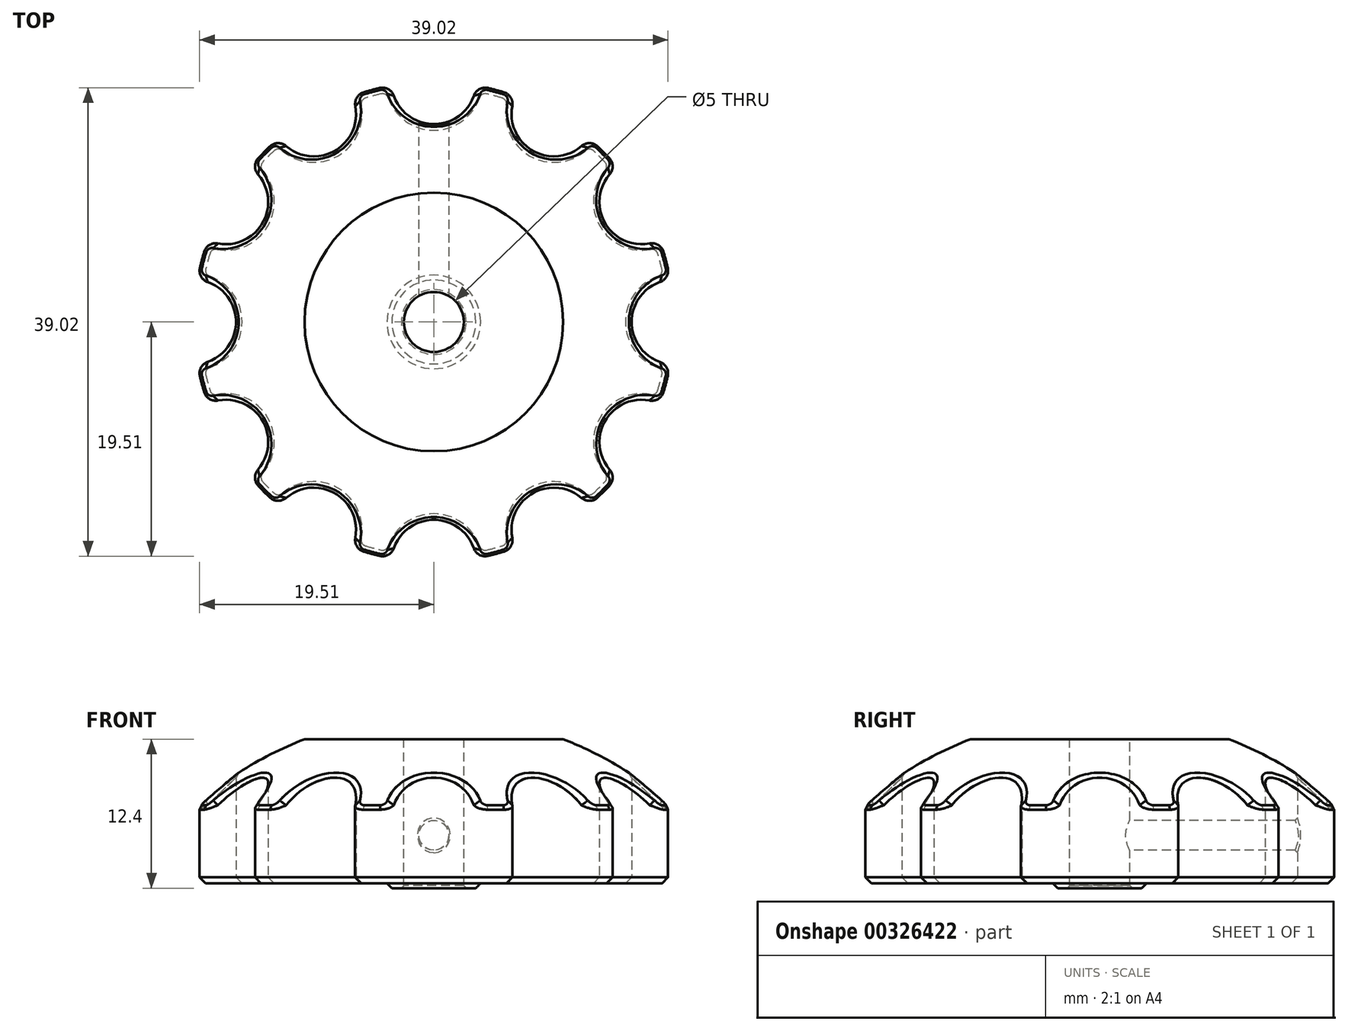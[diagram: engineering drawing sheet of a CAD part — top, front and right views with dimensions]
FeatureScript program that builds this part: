
annotation { "Feature Type Name" : "Feature", "Feature Type Description" : "" }
export const myFeature = defineFeature(function(context is Context, id is Id, definition is map)
    precondition{}
    {
        {
            var Q0;
            Q0=qCreatedBy(makeId("Top.planeOp"),FACE);
            var sketch = newSketch(context, id + "F0", { "sketchPlane" : qUnion([Q0])});
            skLineSegment(sketch, "E0", {"start": v(0, 0) * mm, "end": v(-20, 0) * mm, "construction": true});
            skArc(sketch, "E1", {"start": v(-19.49, -4.5) * mm, "mid": v(-19.32, -5.18) * mm, "end": v(-19.13, -5.85) * mm});
            skArc(sketch, "E2", {"start": v(-18.84, -3.33) * mm, "mid": v(-16.47, 0) * mm, "end": v(-18.84, 3.33) * mm});
            skArc(sketch, "E3", {"start": v(-19.49, 4.5) * mm, "mid": v(-19.39, 3.8) * mm, "end": v(-18.84, 3.33) * mm});
            skPoint(sketch, "E4", {"position": v(-18.84, 3.33) * mm});
            skLineSegment(sketch, "E5", {"start": v(0, 0) * mm, "end": v(-18.51, 4.27) * mm, "construction": true});
            skLineSegment(sketch, "E6.MirrorCS", {"start": v(0, 0) * mm, "end": v(-18.51, -4.27) * mm, "construction": true});
            skArc(sketch, "E7.MirrorCS", {"start": v(-19.49, -4.5) * mm, "mid": v(-19.39, -3.8) * mm, "end": v(-18.84, -3.33) * mm});
            skArc(sketch, "E8.1.0", {"start": v(-19.13, -5.85) * mm, "mid": v(-18.69, -6.41) * mm, "end": v(-17.98, -6.54) * mm});
            skArc(sketch, "E8.1.1", {"start": v(-14.65, -12.3) * mm, "mid": v(-14.27, -8.24) * mm, "end": v(-17.98, -6.54) * mm});
            skArc(sketch, "E8.1.2", {"start": v(-14.63, -13.64) * mm, "mid": v(-14.9, -12.98) * mm, "end": v(-14.65, -12.3) * mm});
            skArc(sketch, "E8.2.0", {"start": v(-13.64, -14.63) * mm, "mid": v(-12.98, -14.9) * mm, "end": v(-12.3, -14.65) * mm});
            skArc(sketch, "E8.2.1", {"start": v(-6.54, -17.98) * mm, "mid": v(-8.24, -14.27) * mm, "end": v(-12.3, -14.65) * mm});
            skArc(sketch, "E8.2.2", {"start": v(-5.85, -19.13) * mm, "mid": v(-6.41, -18.69) * mm, "end": v(-6.54, -17.98) * mm});
            skArc(sketch, "E8.3.0", {"start": v(-4.5, -19.49) * mm, "mid": v(-3.8, -19.39) * mm, "end": v(-3.33, -18.84) * mm});
            skArc(sketch, "E8.3.1", {"start": v(3.33, -18.84) * mm, "mid": v(0, -16.47) * mm, "end": v(-3.33, -18.84) * mm});
            skArc(sketch, "E8.3.2", {"start": v(4.5, -19.49) * mm, "mid": v(3.8, -19.39) * mm, "end": v(3.33, -18.84) * mm});
            skArc(sketch, "E8.4.0", {"start": v(5.85, -19.13) * mm, "mid": v(6.41, -18.69) * mm, "end": v(6.54, -17.98) * mm});
            skArc(sketch, "E8.4.1", {"start": v(12.3, -14.65) * mm, "mid": v(8.24, -14.27) * mm, "end": v(6.54, -17.98) * mm});
            skArc(sketch, "E8.4.2", {"start": v(13.64, -14.63) * mm, "mid": v(12.98, -14.9) * mm, "end": v(12.3, -14.65) * mm});
            skArc(sketch, "E8.5.0", {"start": v(14.63, -13.64) * mm, "mid": v(14.9, -12.98) * mm, "end": v(14.65, -12.3) * mm});
            skArc(sketch, "E8.5.1", {"start": v(17.98, -6.54) * mm, "mid": v(14.27, -8.24) * mm, "end": v(14.65, -12.3) * mm});
            skArc(sketch, "E8.5.2", {"start": v(19.13, -5.85) * mm, "mid": v(18.69, -6.41) * mm, "end": v(17.98, -6.54) * mm});
            skArc(sketch, "E8.6.0", {"start": v(19.49, -4.5) * mm, "mid": v(19.39, -3.8) * mm, "end": v(18.84, -3.33) * mm});
            skArc(sketch, "E8.6.1", {"start": v(18.84, 3.33) * mm, "mid": v(16.47, 0) * mm, "end": v(18.84, -3.33) * mm});
            skArc(sketch, "E8.6.2", {"start": v(19.49, 4.5) * mm, "mid": v(19.39, 3.8) * mm, "end": v(18.84, 3.33) * mm});
            skArc(sketch, "E8.7.0", {"start": v(19.13, 5.85) * mm, "mid": v(18.69, 6.41) * mm, "end": v(17.98, 6.54) * mm});
            skArc(sketch, "E8.7.1", {"start": v(14.65, 12.3) * mm, "mid": v(14.27, 8.24) * mm, "end": v(17.98, 6.54) * mm});
            skArc(sketch, "E8.7.2", {"start": v(14.63, 13.64) * mm, "mid": v(14.9, 12.98) * mm, "end": v(14.65, 12.3) * mm});
            skArc(sketch, "E8.8.0", {"start": v(13.64, 14.63) * mm, "mid": v(12.98, 14.9) * mm, "end": v(12.3, 14.65) * mm});
            skArc(sketch, "E8.8.1", {"start": v(6.54, 17.98) * mm, "mid": v(8.24, 14.27) * mm, "end": v(12.3, 14.65) * mm});
            skArc(sketch, "E8.8.2", {"start": v(5.85, 19.13) * mm, "mid": v(6.41, 18.69) * mm, "end": v(6.54, 17.98) * mm});
            skArc(sketch, "E8.9.0", {"start": v(4.5, 19.49) * mm, "mid": v(3.8, 19.39) * mm, "end": v(3.33, 18.84) * mm});
            skArc(sketch, "E8.9.1", {"start": v(-3.33, 18.84) * mm, "mid": v(0, 16.47) * mm, "end": v(3.33, 18.84) * mm});
            skArc(sketch, "E8.9.2", {"start": v(-4.5, 19.49) * mm, "mid": v(-3.8, 19.39) * mm, "end": v(-3.33, 18.84) * mm});
            skArc(sketch, "E8.10.0", {"start": v(-5.85, 19.13) * mm, "mid": v(-6.41, 18.69) * mm, "end": v(-6.54, 17.98) * mm});
            skArc(sketch, "E8.10.1", {"start": v(-12.3, 14.65) * mm, "mid": v(-8.24, 14.27) * mm, "end": v(-6.54, 17.98) * mm});
            skArc(sketch, "E8.10.2", {"start": v(-13.64, 14.63) * mm, "mid": v(-12.98, 14.9) * mm, "end": v(-12.3, 14.65) * mm});
            skArc(sketch, "E8.11.0", {"start": v(-14.63, 13.64) * mm, "mid": v(-14.9, 12.98) * mm, "end": v(-14.65, 12.3) * mm});
            skArc(sketch, "E8.11.1", {"start": v(-17.98, 6.54) * mm, "mid": v(-14.27, 8.24) * mm, "end": v(-14.65, 12.3) * mm});
            skArc(sketch, "E8.11.2", {"start": v(-19.13, 5.85) * mm, "mid": v(-18.69, 6.41) * mm, "end": v(-17.98, 6.54) * mm});
            skArc(sketch, "E9.trimOffspring", {"start": v(-19.13, 5.85) * mm, "mid": v(-19.32, 5.18) * mm, "end": v(-19.49, 4.5) * mm});
            skArc(sketch, "E10.trimOffspring", {"start": v(-13.64, 14.63) * mm, "mid": v(-14.14, 14.14) * mm, "end": v(-14.63, 13.64) * mm});
            skArc(sketch, "E11.trimOffspring", {"start": v(-4.5, 19.49) * mm, "mid": v(-5.18, 19.32) * mm, "end": v(-5.85, 19.13) * mm});
            skArc(sketch, "E12.trimOffspring", {"start": v(5.85, 19.13) * mm, "mid": v(5.18, 19.32) * mm, "end": v(4.5, 19.49) * mm});
            skArc(sketch, "E13.trimOffspring", {"start": v(14.63, 13.64) * mm, "mid": v(14.14, 14.14) * mm, "end": v(13.64, 14.63) * mm});
            skArc(sketch, "E14.trimOffspring", {"start": v(19.49, 4.5) * mm, "mid": v(19.32, 5.18) * mm, "end": v(19.13, 5.85) * mm});
            skArc(sketch, "E15.trimOffspring", {"start": v(19.13, -5.85) * mm, "mid": v(19.32, -5.18) * mm, "end": v(19.49, -4.5) * mm});
            skArc(sketch, "E16.trimOffspring", {"start": v(13.64, -14.63) * mm, "mid": v(14.14, -14.14) * mm, "end": v(14.63, -13.64) * mm});
            skArc(sketch, "E17.trimOffspring", {"start": v(4.5, -19.49) * mm, "mid": v(5.18, -19.32) * mm, "end": v(5.85, -19.13) * mm});
            skArc(sketch, "E18.trimOffspring", {"start": v(-5.85, -19.13) * mm, "mid": v(-5.18, -19.32) * mm, "end": v(-4.5, -19.49) * mm});
            skArc(sketch, "E19.trimOffspring", {"start": v(-14.63, -13.64) * mm, "mid": v(-14.14, -14.14) * mm, "end": v(-13.64, -14.63) * mm});
            skSolve(sketch);
        }
        {
            var Q0;
            Q0 = qSketchRegion(id + "F0", true);
            extrude(context, id + "F1", {"entities" : qUnion([Q0]), "depth" : 12 * mm});
        }
        {
            var Q0;
            Q0=qCreatedBy(makeId("Front.planeOp"),FACE);
            var sketch = newSketch(context, id + "F2", { "sketchPlane" : qUnion([Q0])});
            skArc(sketch, "E20", {"start": v(25.38, 0) * mm, "mid": v(18.72, 7.44) * mm, "end": v(10, 12.28) * mm});
            skLineSegment(sketch, "E21", {"start": v(0, -16) * mm, "end": v(0, 0) * mm, "construction": true});
            skLineSegment(sketch, "E22", {"start": v(10, 14) * mm, "end": v(30, 14) * mm});
            skLineSegment(sketch, "E23", {"start": v(30, 14) * mm, "end": v(30, 0) * mm});
            skLineSegment(sketch, "E24", {"start": v(10, 12.28) * mm, "end": v(10, 14) * mm});
            skLineSegment(sketch, "E25", {"start": v(25.38, 0) * mm, "end": v(30, 0) * mm});
            skPoint(sketch, "E26.orphan", {"position": v(0, 14) * mm});
            skSolve(sketch);
        }
        {
            var Q0;
            Q0 = qSketchRegion(id + "F2", true);
            var Q1;
            Q1=sQuery(id+"F2.wireOp",EDGE,"E21");
            revolve(context, id + "F3", {"operationType" : NewBodyOperationType.REMOVE, "entities" : qUnion([Q0]), "axis" : qUnion([Q1]), "revolveType" : RevolveType.FULL, "oppositeDirection" : true});
        }
        {
            var Q0;
            Q0=makeQuery(id+"F1.opExtrude","CAP_FACE",FACE,{"disambiguationData":[OSD([sQuery(id+"F0.wireOp",EDGE,"E1"),sQuery(id+"F0.wireOp",EDGE,"E2"),sQuery(id+"F0.wireOp",EDGE,"E3"),sQuery(id+"F0.wireOp",EDGE,"E7.MirrorCS"),sQuery(id+"F0.wireOp",EDGE,"E8.1.0"),sQuery(id+"F0.wireOp",EDGE,"E8.1.1"),sQuery(id+"F0.wireOp",EDGE,"E8.1.2"),sQuery(id+"F0.wireOp",EDGE,"E8.2.0"),sQuery(id+"F0.wireOp",EDGE,"E8.2.1"),sQuery(id+"F0.wireOp",EDGE,"E8.2.2"),sQuery(id+"F0.wireOp",EDGE,"E8.3.0"),sQuery(id+"F0.wireOp",EDGE,"E8.3.1"),sQuery(id+"F0.wireOp",EDGE,"E8.3.2"),sQuery(id+"F0.wireOp",EDGE,"E8.4.0"),sQuery(id+"F0.wireOp",EDGE,"E8.4.1"),sQuery(id+"F0.wireOp",EDGE,"E8.4.2"),sQuery(id+"F0.wireOp",EDGE,"E8.5.0"),sQuery(id+"F0.wireOp",EDGE,"E8.5.1"),sQuery(id+"F0.wireOp",EDGE,"E8.5.2"),sQuery(id+"F0.wireOp",EDGE,"E8.6.0"),sQuery(id+"F0.wireOp",EDGE,"E8.6.1"),sQuery(id+"F0.wireOp",EDGE,"E8.6.2"),sQuery(id+"F0.wireOp",EDGE,"E8.7.0"),sQuery(id+"F0.wireOp",EDGE,"E8.7.1"),sQuery(id+"F0.wireOp",EDGE,"E8.7.2"),sQuery(id+"F0.wireOp",EDGE,"E8.8.0"),sQuery(id+"F0.wireOp",EDGE,"E8.8.1"),sQuery(id+"F0.wireOp",EDGE,"E8.8.2"),sQuery(id+"F0.wireOp",EDGE,"E8.9.0"),sQuery(id+"F0.wireOp",EDGE,"E8.9.1"),sQuery(id+"F0.wireOp",EDGE,"E8.9.2"),sQuery(id+"F0.wireOp",EDGE,"E8.10.0"),sQuery(id+"F0.wireOp",EDGE,"E8.10.1"),sQuery(id+"F0.wireOp",EDGE,"E8.10.2"),sQuery(id+"F0.wireOp",EDGE,"E8.11.0"),sQuery(id+"F0.wireOp",EDGE,"E8.11.1"),sQuery(id+"F0.wireOp",EDGE,"E8.11.2"),sQuery(id+"F0.wireOp",EDGE,"E9.trimOffspring"),sQuery(id+"F0.wireOp",EDGE,"E10.trimOffspring"),sQuery(id+"F0.wireOp",EDGE,"E11.trimOffspring"),sQuery(id+"F0.wireOp",EDGE,"E12.trimOffspring"),sQuery(id+"F0.wireOp",EDGE,"E13.trimOffspring"),sQuery(id+"F0.wireOp",EDGE,"E14.trimOffspring"),sQuery(id+"F0.wireOp",EDGE,"E15.trimOffspring"),sQuery(id+"F0.wireOp",EDGE,"E16.trimOffspring"),sQuery(id+"F0.wireOp",EDGE,"E17.trimOffspring"),sQuery(id+"F0.wireOp",EDGE,"E18.trimOffspring"),sQuery(id+"F0.wireOp",EDGE,"E19.trimOffspring")])],"isStart":false});
            var sketch = newSketch(context, id + "F4", { "sketchPlane" : qUnion([Q0])});
            skCircle(sketch, "E27", {"center": v(0, 0) * mm, "radius": 2.5 * mm});
            skSolve(sketch);
        }
        {
            var Q0;
            Q0=makeQuery(id+"F4.imprint","IMPRINT",FACE,{"disambiguationData":[TD([[makeQuery(id+"F4.imprint","IMPRINT",EDGE,{"derivedFrom":sQuery(id+"F4.wireOp",EDGE,"cDNHE1yy-ZxzA-wdTT-TKaF-RwySO2n7V80O")}),1.0]])]});
            var Q1;
            Q1=makeQuery(id+"F4.imprint","IMPRINT",FACE,{"disambiguationData":[TD([[makeQuery(id+"F4.imprint","IMPRINT",EDGE,{"derivedFrom":sQuery(id+"F4.wireOp",EDGE,"E27")}),1.0]])]});
            extrude(context, id + "F5", {"entities" : qUnion([Q0, Q1]), "operationType" : NewBodyOperationType.REMOVE, "endBound" : BoundingType.THROUGH_ALL, "oppositeDirection" : true, "offsetDistance" : 25 * mm, "depth" : 14 * mm});
        }
        {
            var Q0;
            Q0=qCreatedBy(makeId("Front.planeOp"),FACE);
            var sketch = newSketch(context, id + "F6", { "sketchPlane" : qUnion([Q0])});
            skLineSegment(sketch, "E28.bottom", {"start": v(-2.5, 0) * mm, "end": v(-3.5, 0) * mm});
            skLineSegment(sketch, "E28.top", {"start": v(-2.5, -0.4) * mm, "end": v(-3.5, -0.4) * mm});
            skLineSegment(sketch, "E28.left", {"start": v(-2.5, 0) * mm, "end": v(-2.5, -0.4) * mm});
            skLineSegment(sketch, "E28.right", {"start": v(-3.5, 0) * mm, "end": v(-3.5, -0.4) * mm, "construction": true});
            skLineSegment(sketch, "E29", {"start": v(-3.5, -0.4) * mm, "end": v(-3.9, 0) * mm});
            skLineSegment(sketch, "E30", {"start": v(-3.5, 0) * mm, "end": v(-3.9, 0) * mm});
            skSolve(sketch);
        }
        {
            var Q0;
            Q0 = qSketchRegion(id + "F6", true);
            var Q1;
            Q1=makeQuery(id+"F5.boolean.opBoolean","COPY",FACE,{"derivedFrom":makeQuery(id+"F5.opExtrude","SWEPT_FACE",FACE,{"disambiguationData":[OSD([sQuery(id+"F4.wireOp",EDGE,"E27")])]})});
            revolve(context, id + "F7", {"operationType" : NewBodyOperationType.ADD, "surfaceOperationType" : NewSurfaceOperationType.NEW, "entities" : qUnion([Q0]), "axis" : qUnion([Q1]), "revolveType" : RevolveType.FULL});
        }
        {
            var Q0;
            Q0=qCreatedBy(makeId("Front.planeOp"),FACE);
            var sketch = newSketch(context, id + "F8", { "sketchPlane" : qUnion([Q0])});
            skLineSegment(sketch, "E31", {"start": v(0, 0) * mm, "end": v(0, 4) * mm});
            skCircle(sketch, "E32", {"center": v(0, 4) * mm, "radius": 1.25 * mm});
            skSolve(sketch);
        }
        {
            var Q0;
            Q0 = qSketchRegion(id + "F8", true);
            extrude(context, id + "F9", {"entities" : qUnion([Q0]), "operationType" : NewBodyOperationType.REMOVE, "endBound" : BoundingType.THROUGH_ALL, "oppositeDirection" : true, "depth" : 25 * mm, "offsetDistance" : 25 * mm});
        }
        {
            var Q0;
            Q0=makeQuery(id+"F7.opRevolve","SWEPT_EDGE",EDGE,{"disambiguationData":[OSD([sQuery(id+"F6.wireOp",EDGE,"E28.top"),sQuery(id+"F6.wireOp",EDGE,"E28.left")])]});
            var Q1;
            Q1=makeQuery(id+"F9.boolean.opBoolean","INTERSECT",EDGE,{"derivedFrom":[makeQuery(id+"F1.opExtrude","SWEPT_FACE",FACE,{"disambiguationData":[OSD([sQuery(id+"F0.wireOp",EDGE,"E8.9.1")])]}),makeQuery(id+"F9.opExtrude","SWEPT_FACE",FACE,{"disambiguationData":[OSD([sQuery(id+"F8.wireOp",EDGE,"E32")])]})]});
            chamfer(context, id + "F10", {"entities" : qUnion([Q0, Q1]), "width" : 0.2 * mm, "tangentPropagation" : true});
        }
        {
            var Q0;
            Q0=makeQuery(id+"F3.boolean.opBoolean","INTERSECT",EDGE,{"derivedFrom":[makeQuery(id+"F1.opExtrude","SWEPT_FACE",FACE,{"disambiguationData":[OSD([sQuery(id+"F0.wireOp",EDGE,"E8.3.1")])]}),makeQuery(id+"F3.opRevolve","SWEPT_FACE",FACE,{"disambiguationData":[OSD([sQuery(id+"F2.wireOp",EDGE,"E20")])]})]});
            var Q1;
            Q1=makeQuery(id+"F1.opExtrude","CAP_EDGE",EDGE,{"disambiguationData":[OSD([sQuery(id+"F0.wireOp",EDGE,"E8.1.1")])],"isStart":true});
            var Q2;
            Q2=makeQuery(id+"F5.boolean.opBoolean","COPY",EDGE,{"derivedFrom":makeQuery(id+"F5.opExtrude","CAP_EDGE",EDGE,{"disambiguationData":[OSD([sQuery(id+"F4.wireOp",EDGE,"E27")])],"isStart":true})});
            chamfer(context, id + "F11", {"entities" : qUnion([Q0, Q1, Q2]), "width" : 0.5 * mm, "tangentPropagation" : true});
        }
    });
